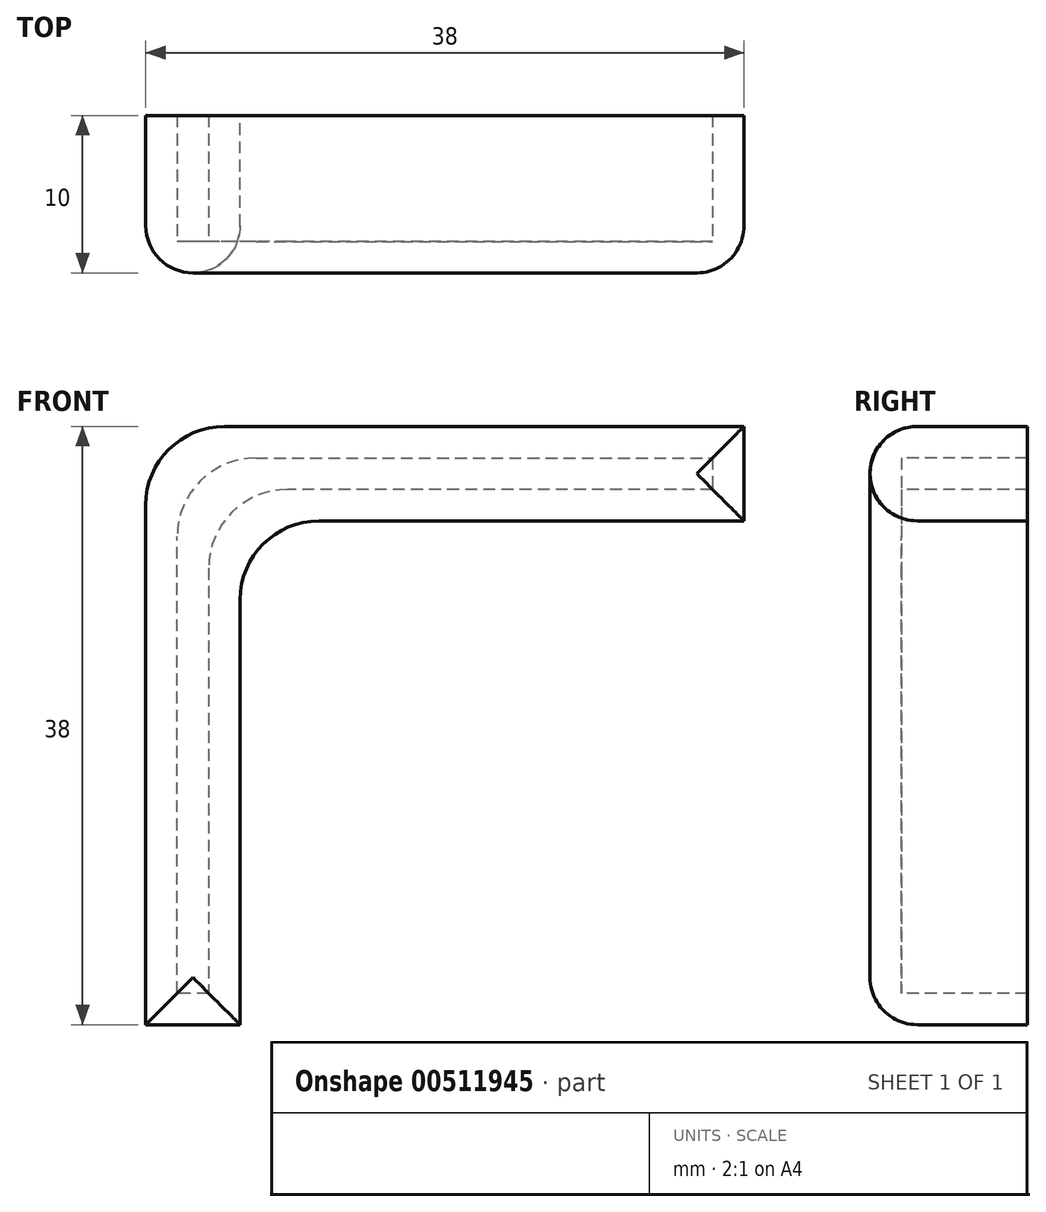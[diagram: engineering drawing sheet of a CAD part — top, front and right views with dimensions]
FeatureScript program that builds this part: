
annotation { "Feature Type Name" : "Feature", "Feature Type Description" : "" }
export const myFeature = defineFeature(function(context is Context, id is Id, definition is map)
    precondition{}
    {
        {
            var Q0;
            Q0=qCreatedBy(makeId("Front.planeOp"),FACE);
            var sketch = newSketch(context, id + "F0", { "sketchPlane" : qUnion([Q0])});
            skLineSegment(sketch, "E0", {"start": v(0, 0) * mm, "end": v(38, 0) * mm});
            skLineSegment(sketch, "E1", {"start": v(38, 0) * mm, "end": v(38, -6) * mm});
            skLineSegment(sketch, "E2", {"start": v(38, -6) * mm, "end": v(6, -6) * mm});
            skLineSegment(sketch, "E3", {"start": v(6, -6) * mm, "end": v(6, -38) * mm});
            skLineSegment(sketch, "E4", {"start": v(6, -38) * mm, "end": v(0, -38) * mm});
            skLineSegment(sketch, "E5", {"start": v(0, -38) * mm, "end": v(0, 0) * mm});
            skSolve(sketch);
        }
        {
            var Q0;
            Q0=makeQuery(id+"F0.imprint","IMPRINT",FACE,{"disambiguationData":[TD([[makeQuery(id+"F0.imprint","IMPRINT",EDGE,{"derivedFrom":sQuery(id+"F0.wireOp",EDGE,"E0")}),-1.0]])]});
            var Q1;
            Q1 = qSketchRegion(id + "F0", true);
            extrude(context, id + "F1", {"entities" : qUnion([Q0, Q1]), "depth" : 10 * mm});
        }
        {
            var Q0;
            Q0=qCreatedBy(makeId("Front.planeOp"),FACE);
            var sketch = newSketch(context, id + "F2", { "sketchPlane" : qUnion([Q0])});
            skLineSegment(sketch, "E6", {"start": v(2, -2) * mm, "end": v(36, -2) * mm});
            skLineSegment(sketch, "E7", {"start": v(36, -2) * mm, "end": v(36, -4) * mm});
            skLineSegment(sketch, "E8", {"start": v(36, -4) * mm, "end": v(4, -4) * mm});
            skLineSegment(sketch, "E9", {"start": v(4, -4) * mm, "end": v(4, -36) * mm});
            skLineSegment(sketch, "E10", {"start": v(4, -36) * mm, "end": v(2, -36) * mm});
            skLineSegment(sketch, "E11", {"start": v(2, -36) * mm, "end": v(2, -2) * mm});
            skSolve(sketch);
        }
        {
            var Q0;
            Q0 = qSketchRegion(id + "F2", true);
            extrude(context, id + "F3", {"entities" : qUnion([Q0]), "operationType" : NewBodyOperationType.REMOVE, "oppositeDirection" : true, "depth" : 10 * mm, "hasSecondDirection" : true, "secondDirectionOppositeDirection" : false, "secondDirectionDepth" : 8 * mm});
        }
        {
            var Q0;
            Q0=makeQuery(id+"F1.opExtrude","SWEPT_EDGE",EDGE,{"disambiguationData":[OSD([sQuery(id+"F0.wireOp",EDGE,"E0"),sQuery(id+"F0.wireOp",EDGE,"E5")])]});
            var Q1;
            Q1=makeQuery(id+"F3.boolean.opBoolean","COPY",EDGE,{"derivedFrom":makeQuery(id+"F3.opExtrude","SWEPT_EDGE",EDGE,{"disambiguationData":[OSD([sQuery(id+"F2.wireOp",EDGE,"E8"),sQuery(id+"F2.wireOp",EDGE,"E9")])]})});
            var Q2;
            Q2=makeQuery(id+"F3.boolean.opBoolean","COPY",EDGE,{"derivedFrom":makeQuery(id+"F3.opExtrude","SWEPT_EDGE",EDGE,{"disambiguationData":[OSD([sQuery(id+"F2.wireOp",EDGE,"E6"),sQuery(id+"F2.wireOp",EDGE,"E11")])]})});
            var Q3;
            Q3=makeQuery(id+"F1.opExtrude","SWEPT_EDGE",EDGE,{"disambiguationData":[OSD([sQuery(id+"F0.wireOp",EDGE,"E2"),sQuery(id+"F0.wireOp",EDGE,"E3")])]});
            fillet(context, id + "F4", {"entities" : qUnion([Q0, Q1, Q2, Q3]), "radius" : 5 * mm, "tangentPropagation" : true, "allowEdgeOverflow" : false});
        }
        {
            var Q0;
            Q0=makeQuery(id+"F1.opExtrude","CAP_EDGE",EDGE,{"disambiguationData":[OSD([sQuery(id+"F0.wireOp",EDGE,"E4")])],"isStart":false});
            var Q1;
            Q1=makeQuery(id+"F1.opExtrude","CAP_EDGE",EDGE,{"disambiguationData":[OSD([sQuery(id+"F0.wireOp",EDGE,"E3")])],"isStart":false});
            var Q2;
            Q2=makeQuery(id+"F1.opExtrude","CAP_EDGE",EDGE,{"disambiguationData":[OSD([sQuery(id+"F0.wireOp",EDGE,"E0")])],"isStart":false});
            var Q3;
            Q3=makeQuery(id+"F1.opExtrude","CAP_EDGE",EDGE,{"disambiguationData":[OSD([sQuery(id+"F0.wireOp",EDGE,"E1")])],"isStart":false});
            fillet(context, id + "F5", {"entities" : qUnion([Q0, Q1, Q2, Q3]), "radius" : 3 * mm, "tangentPropagation" : true, "allowEdgeOverflow" : false});
        }
    });
